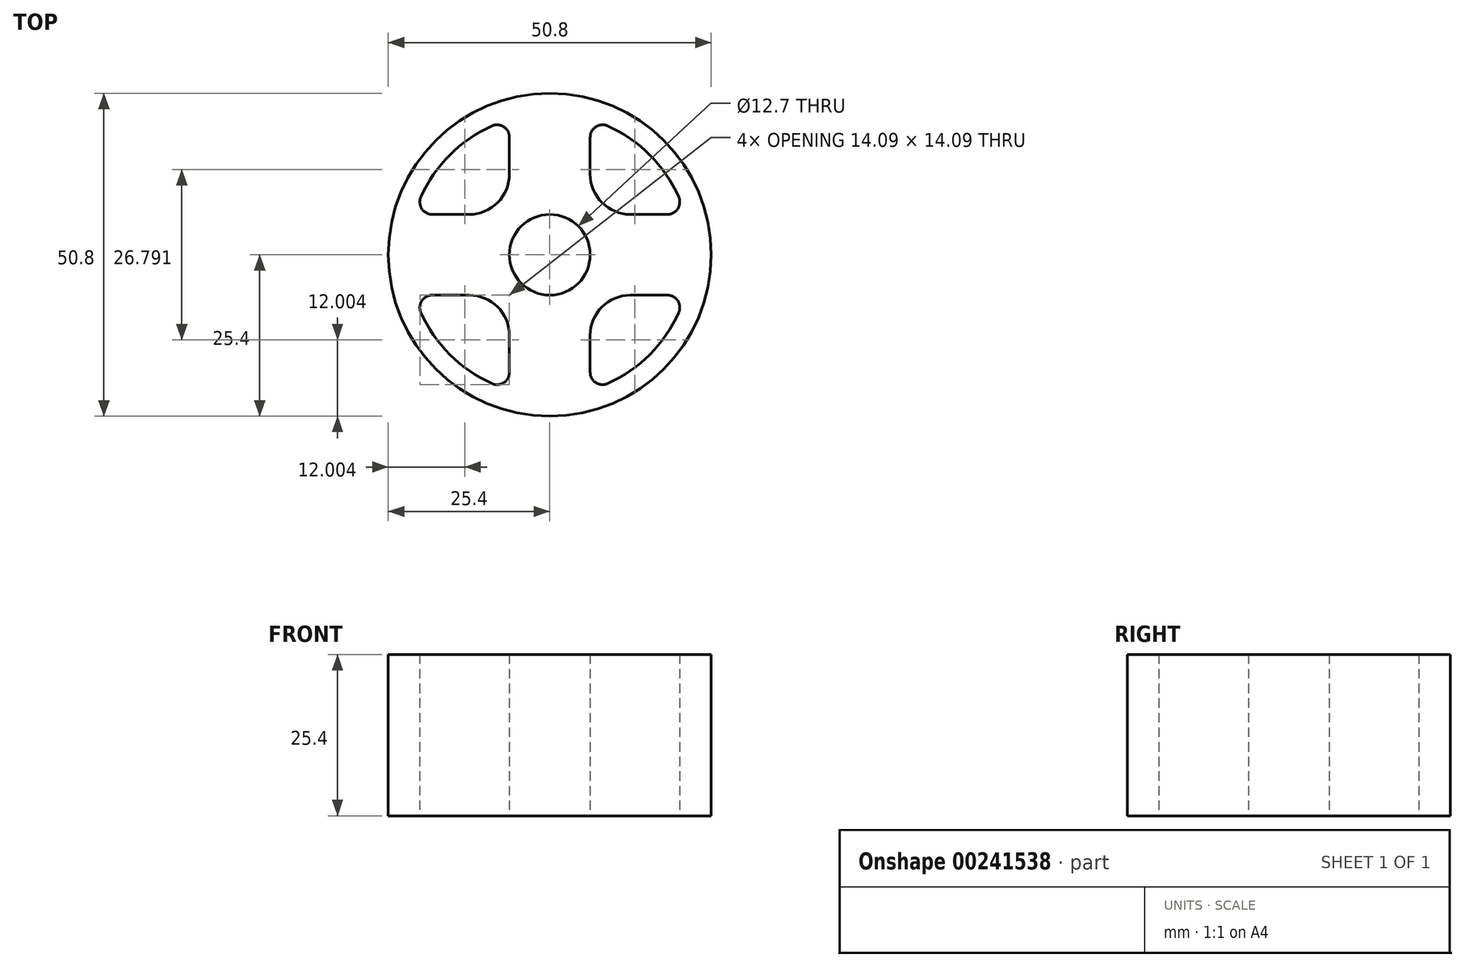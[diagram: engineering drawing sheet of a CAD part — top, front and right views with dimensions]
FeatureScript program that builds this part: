
annotation { "Feature Type Name" : "Feature", "Feature Type Description" : "" }
export const myFeature = defineFeature(function(context is Context, id is Id, definition is map)
    precondition{}
    {
        {
            var Q0;
            Q0=qCreatedBy(makeId("Top.planeOp"),FACE);
            var sketch = newSketch(context, id + "F0", { "sketchPlane" : qUnion([Q0])});
            skCircle(sketch, "E0", {"center": v(0, 0) * mm, "radius": 6.35 * mm});
            skCircle(sketch, "E1", {"center": v(0, 0) * mm, "radius": 25.4 * mm});
            skArc(sketch, "E2", {"start": v(-9.1, 20.28) * mm, "mid": v(-15.72, 15.72) * mm, "end": v(-20.28, 9.1) * mm});
            skLineSegment(sketch, "E3", {"start": v(0, 0) * mm, "end": v(0, 22.23) * mm});
            skLineSegment(sketch, "E4.0", {"start": v(6.35, 12.7) * mm, "end": v(6.35, 18.5) * mm});
            skLineSegment(sketch, "E5.0", {"start": v(-6.35, 12.7) * mm, "end": v(-6.35, 18.5) * mm});
            skLineSegment(sketch, "E6", {"start": v(0, 0) * mm, "end": v(22.23, 0) * mm});
            skLineSegment(sketch, "E7.0", {"start": v(12.7, -6.35) * mm, "end": v(18.5, -6.35) * mm});
            skLineSegment(sketch, "E8.0", {"start": v(12.7, 6.35) * mm, "end": v(18.5, 6.35) * mm});
            skLineSegment(sketch, "E9", {"start": v(0, 0) * mm, "end": v(0, -22.23) * mm});
            skLineSegment(sketch, "E10.0", {"start": v(-6.35, -12.7) * mm, "end": v(-6.35, -18.5) * mm});
            skLineSegment(sketch, "E11.0", {"start": v(6.35, -12.7) * mm, "end": v(6.35, -18.5) * mm});
            skLineSegment(sketch, "E12", {"start": v(0, 0) * mm, "end": v(-22.23, 0) * mm});
            skLineSegment(sketch, "E13.0", {"start": v(-12.7, 6.35) * mm, "end": v(-18.5, 6.35) * mm});
            skLineSegment(sketch, "E14.0", {"start": v(-12.7, -6.35) * mm, "end": v(-18.5, -6.35) * mm});
            skArc(sketch, "E15.trimOffspring", {"start": v(20.28, 9.1) * mm, "mid": v(15.72, 15.72) * mm, "end": v(9.1, 20.28) * mm});
            skArc(sketch, "E16.trimOffspring", {"start": v(9.1, -20.28) * mm, "mid": v(15.72, -15.72) * mm, "end": v(20.28, -9.1) * mm});
            skArc(sketch, "E17.trimOffspring", {"start": v(-20.28, -9.1) * mm, "mid": v(-15.72, -15.72) * mm, "end": v(-9.1, -20.28) * mm});
            skPoint(sketch, "E18.visualSharp", {"position": v(6.35, 6.35) * mm});
            skArc(sketch, "E18.filletArc", {"start": v(6.35, 12.7) * mm, "mid": v(8.2, 8.2) * mm, "end": v(12.7, 6.35) * mm});
            skPoint(sketch, "E19.visualSharp", {"position": v(-6.35, 6.35) * mm});
            skArc(sketch, "E19.filletArc", {"start": v(-12.7, 6.35) * mm, "mid": v(-8.2, 8.2) * mm, "end": v(-6.35, 12.7) * mm});
            skPoint(sketch, "E20.visualSharp", {"position": v(-6.35, -6.35) * mm});
            skArc(sketch, "E20.filletArc", {"start": v(-6.35, -12.7) * mm, "mid": v(-8.2, -8.2) * mm, "end": v(-12.7, -6.35) * mm});
            skPoint(sketch, "E21.visualSharp", {"position": v(6.35, -6.35) * mm});
            skArc(sketch, "E21.filletArc", {"start": v(12.7, -6.35) * mm, "mid": v(8.2, -8.2) * mm, "end": v(6.35, -12.7) * mm});
            skPoint(sketch, "E22.visualSharp", {"position": v(-6.35, 21.3) * mm});
            skArc(sketch, "E22.filletArc", {"start": v(-6.35, 18.5) * mm, "mid": v(-7.24, 20.13) * mm, "end": v(-9.1, 20.28) * mm});
            skPoint(sketch, "E23.visualSharp", {"position": v(-21.3, 6.35) * mm});
            skArc(sketch, "E23.filletArc", {"start": v(-20.28, 9.1) * mm, "mid": v(-20.13, 7.24) * mm, "end": v(-18.5, 6.35) * mm});
            skPoint(sketch, "E24.visualSharp", {"position": v(6.35, 21.3) * mm});
            skArc(sketch, "E24.filletArc", {"start": v(9.1, 20.28) * mm, "mid": v(7.24, 20.13) * mm, "end": v(6.35, 18.5) * mm});
            skPoint(sketch, "E25.visualSharp", {"position": v(21.3, 6.35) * mm});
            skArc(sketch, "E25.filletArc", {"start": v(18.5, 6.35) * mm, "mid": v(20.13, 7.24) * mm, "end": v(20.28, 9.1) * mm});
            skPoint(sketch, "E26.visualSharp", {"position": v(21.3, -6.35) * mm});
            skArc(sketch, "E26.filletArc", {"start": v(20.28, -9.1) * mm, "mid": v(20.13, -7.24) * mm, "end": v(18.5, -6.35) * mm});
            skPoint(sketch, "E27.visualSharp", {"position": v(6.35, -21.3) * mm});
            skArc(sketch, "E27.filletArc", {"start": v(6.35, -18.5) * mm, "mid": v(7.24, -20.13) * mm, "end": v(9.1, -20.28) * mm});
            skPoint(sketch, "E28.visualSharp", {"position": v(-6.35, -21.3) * mm});
            skArc(sketch, "E28.filletArc", {"start": v(-9.1, -20.28) * mm, "mid": v(-7.24, -20.13) * mm, "end": v(-6.35, -18.5) * mm});
            skPoint(sketch, "E29.visualSharp", {"position": v(-21.3, -6.35) * mm});
            skArc(sketch, "E29.filletArc", {"start": v(-18.5, -6.35) * mm, "mid": v(-20.13, -7.24) * mm, "end": v(-20.28, -9.1) * mm});
            skSolve(sketch);
        }
        {
            var Q0;
            Q0 = qSketchRegion(id + "F0", true);
            extrude(context, id + "F1", {"entities" : qUnion([Q0]), "endBound" : BoundingType.SYMMETRIC, "depth" : 25.4 * mm});
        }
    });
